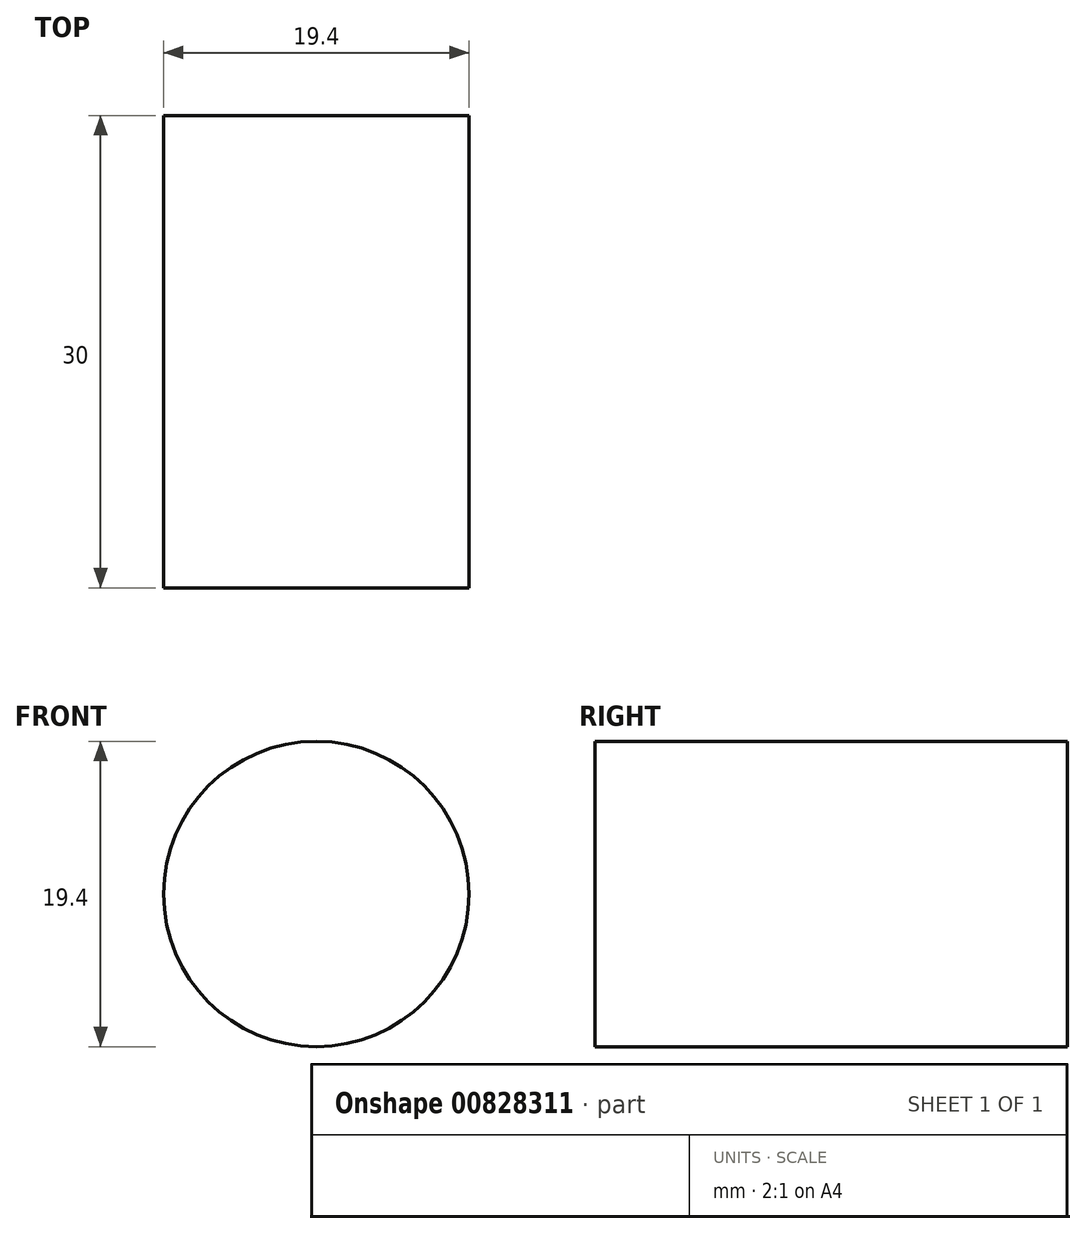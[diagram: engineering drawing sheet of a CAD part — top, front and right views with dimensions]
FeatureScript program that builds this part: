
annotation { "Feature Type Name" : "Feature", "Feature Type Description" : "" }
export const myFeature = defineFeature(function(context is Context, id is Id, definition is map)
    precondition{}
    {
        {
            var Q0;
            Q0=qCreatedBy(makeId("Front.planeOp"),FACE);
            var sketch = newSketch(context, id + "F0", { "sketchPlane" : qUnion([Q0])});
            skCircle(sketch, "E0", {"center": v(-21.44, 11.86) * mm, "radius": 9.7 * mm});
            skSolve(sketch);
        }
        {
            var Q0;
            Q0 = qSketchRegion(id + "F0", true);
            extrude(context, id + "F1", {"entities" : qUnion([Q0]), "depth" : 30 * mm, "offsetDistance" : 25 * mm});
        }
    });
